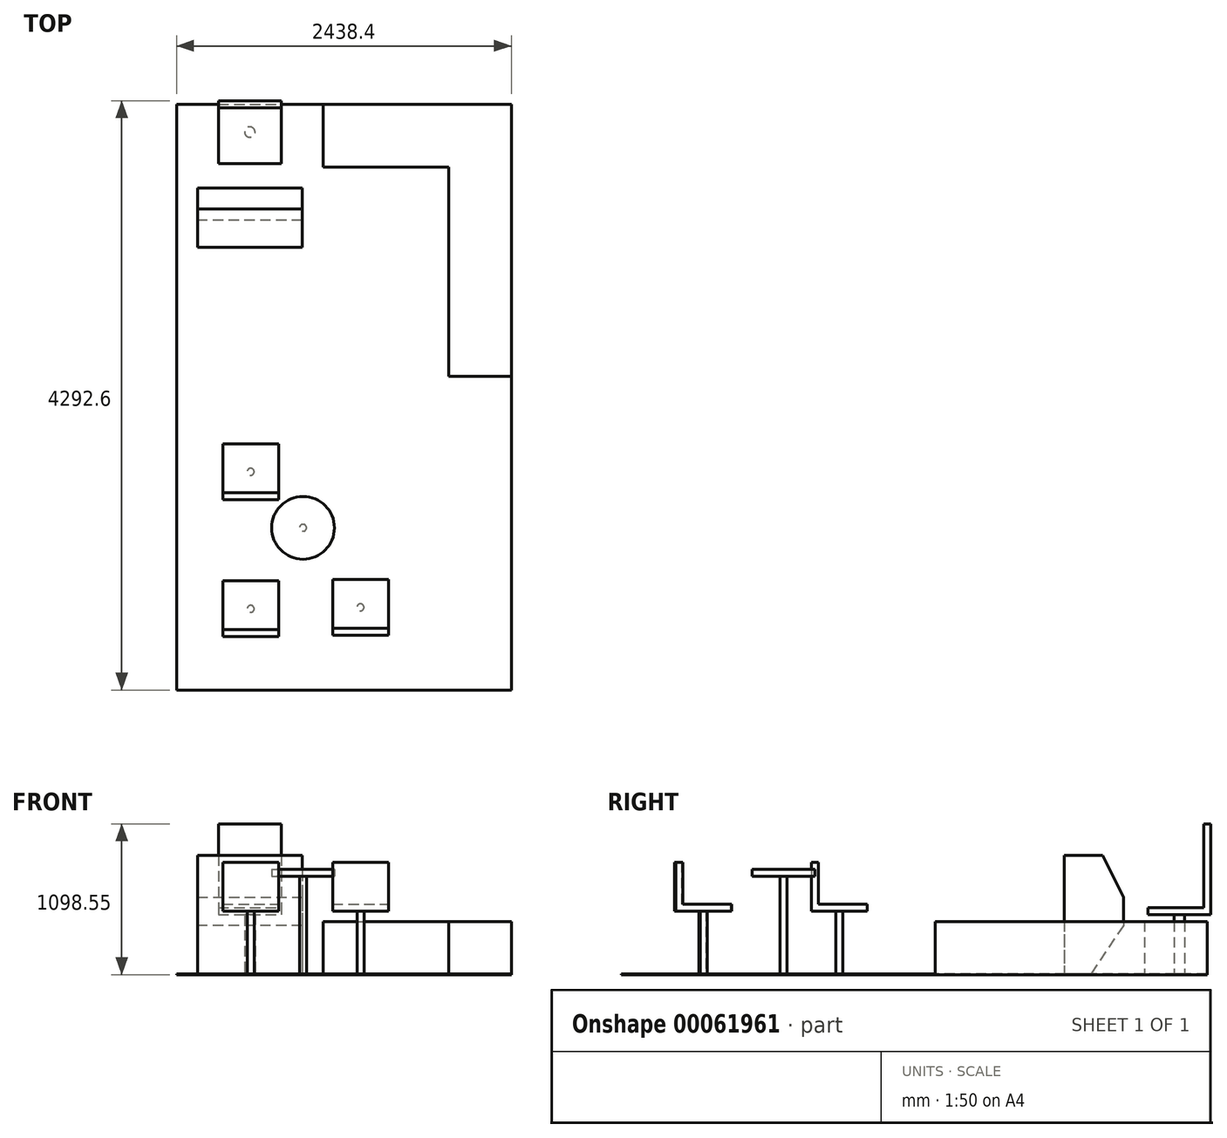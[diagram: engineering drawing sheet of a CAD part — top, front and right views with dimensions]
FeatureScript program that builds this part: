
annotation { "Feature Type Name" : "Feature", "Feature Type Description" : "" }
export const myFeature = defineFeature(function(context is Context, id is Id, definition is map)
    precondition{}
    {
        {
            var Q0;
            Q0=qCreatedBy(makeId("Top.planeOp"),FACE);
            var sketch = newSketch(context, id + "F0", { "sketchPlane" : qUnion([Q0])});
            skLineSegment(sketch, "E0.bottom", {"start": v(-2438.4, 4267.2) * mm, "end": v(0, 4267.2) * mm});
            skLineSegment(sketch, "E0.top", {"start": v(-2438.4, 0) * mm, "end": v(0, 0) * mm});
            skLineSegment(sketch, "E0.left", {"start": v(-2438.4, 4267.2) * mm, "end": v(-2438.4, 0) * mm});
            skLineSegment(sketch, "E0.right", {"start": v(0, 4267.2) * mm, "end": v(0, 0) * mm});
            skSolve(sketch);
        }
        {
            var Q0;
            Q0 = qSketchRegion(id + "F0", true);
            var Q1;
            Q1=makeQuery(id+"F0.imprint","IMPRINT",FACE,{"disambiguationData":[TD([[makeQuery(id+"F0.imprint","IMPRINT",EDGE,{"derivedFrom":sQuery(id+"F0.wireOp",EDGE,"E0.bottom")}),-1.0]])]});
            extrude(context, id + "F1", {"entities" : qUnion([Q0, Q1]), "depth" : 6.35 * mm});
        }
        {
            var Q0;
            Q0=makeQuery(id+"F1.opExtrude","CAP_FACE",FACE,{"disambiguationData":[OSD([sQuery(id+"F0.wireOp",EDGE,"E0.bottom"),sQuery(id+"F0.wireOp",EDGE,"E0.top"),sQuery(id+"F0.wireOp",EDGE,"E0.left"),sQuery(id+"F0.wireOp",EDGE,"E0.right")])],"isStart":false});
            var sketch = newSketch(context, id + "F2", { "sketchPlane" : qUnion([Q0])});
            skLineSegment(sketch, "E1.bottom", {"start": v(0, 4267.2) * mm, "end": v(-457.2, 4267.2) * mm});
            skLineSegment(sketch, "E1.top", {"start": v(0, 2286) * mm, "end": v(-457.2, 2286) * mm});
            skLineSegment(sketch, "E1.left", {"start": v(0, 4267.2) * mm, "end": v(0, 2286) * mm});
            skLineSegment(sketch, "E1.right", {"start": v(-457.2, 4267.2) * mm, "end": v(-457.2, 2286) * mm});
            skLineSegment(sketch, "E2.bottom", {"start": v(-1371.6, 4267.2) * mm, "end": v(-457.2, 4267.2) * mm});
            skLineSegment(sketch, "E2.top", {"start": v(-1371.6, 3810) * mm, "end": v(-457.2, 3810) * mm});
            skLineSegment(sketch, "E2.left", {"start": v(-1371.6, 4267.2) * mm, "end": v(-1371.6, 3810) * mm});
            skLineSegment(sketch, "E2.right", {"start": v(-457.2, 4267.2) * mm, "end": v(-457.2, 3810) * mm});
            skSolve(sketch);
        }
        {
            var Q0;
            Q0 = qSketchRegion(id + "F2", true);
            extrude(context, id + "F3", {"entities" : qUnion([Q0]), "operationType" : NewBodyOperationType.ADD, "depth" : 381 * mm});
        }
        {
            var Q0;
            Q0=makeQuery(id+"F1.opExtrude","CAP_FACE",FACE,{"disambiguationData":[OSD([sQuery(id+"F0.wireOp",EDGE,"E0.bottom"),sQuery(id+"F0.wireOp",EDGE,"E0.top"),sQuery(id+"F0.wireOp",EDGE,"E0.left"),sQuery(id+"F0.wireOp",EDGE,"E0.right")])],"isStart":false});
            var sketch = newSketch(context, id + "F4", { "sketchPlane" : qUnion([Q0])});
            skLineSegment(sketch, "E3.bottom", {"start": v(-2286, 3657.6) * mm, "end": v(-1524, 3657.6) * mm});
            skLineSegment(sketch, "E3.top", {"start": v(-2286, 3225.8) * mm, "end": v(-1524, 3225.8) * mm});
            skLineSegment(sketch, "E3.left", {"start": v(-2286, 3657.6) * mm, "end": v(-2286, 3225.8) * mm});
            skLineSegment(sketch, "E3.right", {"start": v(-1524, 3657.6) * mm, "end": v(-1524, 3225.8) * mm});
            skSolve(sketch);
        }
        {
            var Q0;
            Q0 = qSketchRegion(id + "F4", true);
            extrude(context, id + "F5", {"entities" : qUnion([Q0]), "operationType" : NewBodyOperationType.ADD, "depth" : 863.6 * mm});
        }
        {
            var Q0;
            Q0=makeQuery(id+"F5.opExtrude","CAP_EDGE",EDGE,{"disambiguationData":[OSD([sQuery(id+"F4.wireOp",EDGE,"E3.bottom")])],"isStart":false});
            chamfer(context, id + "F6", {"entities" : qUnion([Q0]), "chamferType" : ChamferType.TWO_OFFSETS, "width1" : 304.8 * mm, "oppositeDirection" : false, "width2" : 152.4 * mm, "tangentPropagation" : true});
        }
        {
            var Q0;
            Q0=makeQuery(id+"F5.opExtrude","SWEPT_FACE",FACE,{"disambiguationData":[OSD([sQuery(id+"F4.wireOp",EDGE,"E3.left")])]});
            var sketch = newSketch(context, id + "F7", { "sketchPlane" : qUnion([Q0])});
            skLineSegment(sketch, "E4.0", {"start": v(-3657.6, 565.15) * mm, "end": v(-3657.6, 6.35) * mm});
            skLineSegment(sketch, "E5.0", {"start": v(-3225.8, 869.95) * mm, "end": v(-3225.8, 6.35) * mm});
            skLineSegment(sketch, "E6.0", {"start": v(-3657.6, 6.35) * mm, "end": v(-3225.8, 6.35) * mm});
            skLineSegment(sketch, "E7", {"start": v(-3657.6, 356.85) * mm, "end": v(-3421.3, 6.35) * mm});
            skSolve(sketch);
        }
        {
            var Q0;
            {var subQ3=sQuery(id+"F7.wireOp",EDGE,"E7");Q0=makeQuery(id+"F7.imprint","IMPRINT",FACE,{"disambiguationData":[TD([[makeQuery(id+"F7.imprint","IMPRINT",EDGE,{"derivedFrom":subQ3}),-1.0]])]});}
            extrude(context, id + "F8", {"entities" : qUnion([Q0]), "operationType" : NewBodyOperationType.REMOVE, "oppositeDirection" : true, "depth" : 762 * mm});
        }
        {
            var Q0;
            Q0=makeQuery(id+"F8.boolean.opBoolean","MERGE",FACE,{"derivedFrom":[makeQuery(id+"F1.opExtrude","CAP_FACE",FACE,{"disambiguationData":[OSD([sQuery(id+"F0.wireOp",EDGE,"E0.bottom"),sQuery(id+"F0.wireOp",EDGE,"E0.top"),sQuery(id+"F0.wireOp",EDGE,"E0.left"),sQuery(id+"F0.wireOp",EDGE,"E0.right")])],"isStart":false}),makeQuery(id+"F8.opExtrude","SWEPT_FACE",FACE,{"disambiguationData":[OSD([sQuery(id+"F7.wireOp",EDGE,"E6.0")])]})]});
            var sketch = newSketch(context, id + "F9", { "sketchPlane" : qUnion([Q0])});
            skCircle(sketch, "E8", {"center": v(-1905, 4064) * mm, "radius": 38.1 * mm});
            skLineSegment(sketch, "E9", {"start": v(-1905, 3225.8) * mm, "end": v(-1905, 4064) * mm});
            skLineSegment(sketch, "E10.0", {"start": v(-1524, 3657.6) * mm, "end": v(-2286, 3657.6) * mm});
            skSolve(sketch);
        }
        {
            var Q0;
            Q0 = qSketchRegion(id + "F9", true);
            extrude(context, id + "F10", {"entities" : qUnion([Q0]), "operationType" : NewBodyOperationType.ADD, "depth" : 431.8 * mm});
        }
        {
            var Q0;
            Q0=makeQuery(id+"F10.opExtrude","CAP_FACE",FACE,{"disambiguationData":[OSD([sQuery(id+"F9.wireOp",EDGE,"E8")])],"isStart":false});
            var sketch = newSketch(context, id + "F11", { "sketchPlane" : qUnion([Q0])});
            skLineSegment(sketch, "E11.rect.bottom", {"start": v(-2133.6, 4292.6) * mm, "end": v(-1676.4, 4292.6) * mm});
            skLineSegment(sketch, "E11.rect.top", {"start": v(-2133.6, 3835.4) * mm, "end": v(-1676.4, 3835.4) * mm});
            skLineSegment(sketch, "E11.rect.left", {"start": v(-2133.6, 4292.6) * mm, "end": v(-2133.6, 3835.4) * mm});
            skLineSegment(sketch, "E11.rect.right", {"start": v(-1676.4, 4292.6) * mm, "end": v(-1676.4, 3835.4) * mm});
            skPoint(sketch, "E11.rect.middle", {"position": v(-1905, 4064) * mm});
            skSolve(sketch);
        }
        {
            var Q0;
            Q0 = qSketchRegion(id + "F11", true);
            extrude(context, id + "F12", {"entities" : qUnion([Q0]), "operationType" : NewBodyOperationType.ADD, "depth" : 50.8 * mm});
        }
        {
            var Q0;
            Q0=makeQuery(id+"F12.opExtrude","CAP_FACE",FACE,{"disambiguationData":[OSD([sQuery(id+"F11.wireOp",EDGE,"E11.rect.bottom"),sQuery(id+"F11.wireOp",EDGE,"E11.rect.top"),sQuery(id+"F11.wireOp",EDGE,"E11.rect.left"),sQuery(id+"F11.wireOp",EDGE,"E11.rect.right")])],"isStart":false});
            var sketch = newSketch(context, id + "F13", { "sketchPlane" : qUnion([Q0])});
            skLineSegment(sketch, "E12.bottom", {"start": v(-2133.6, 4292.6) * mm, "end": v(-1676.4, 4292.6) * mm});
            skLineSegment(sketch, "E12.top", {"start": v(-2133.6, 4241.8) * mm, "end": v(-1676.4, 4241.8) * mm});
            skLineSegment(sketch, "E12.left", {"start": v(-2133.6, 4292.6) * mm, "end": v(-2133.6, 4241.8) * mm});
            skLineSegment(sketch, "E12.right", {"start": v(-1676.4, 4292.6) * mm, "end": v(-1676.4, 4241.8) * mm});
            skSolve(sketch);
        }
        {
            var Q0;
            Q0 = qSketchRegion(id + "F13", true);
            extrude(context, id + "F14", {"entities" : qUnion([Q0]), "operationType" : NewBodyOperationType.ADD, "depth" : 609.6 * mm});
        }
        {
            var Q0;
            Q0=makeQuery(id+"F8.boolean.opBoolean","MERGE",FACE,{"derivedFrom":[makeQuery(id+"F1.opExtrude","CAP_FACE",FACE,{"disambiguationData":[OSD([sQuery(id+"F0.wireOp",EDGE,"E0.bottom"),sQuery(id+"F0.wireOp",EDGE,"E0.top"),sQuery(id+"F0.wireOp",EDGE,"E0.left"),sQuery(id+"F0.wireOp",EDGE,"E0.right")])],"isStart":false}),makeQuery(id+"F8.opExtrude","SWEPT_FACE",FACE,{"disambiguationData":[OSD([sQuery(id+"F7.wireOp",EDGE,"E6.0")])]})]});
            var sketch = newSketch(context, id + "F15", { "sketchPlane" : qUnion([Q0])});
            skCircle(sketch, "E13", {"center": v(-1898.37, 1589.52) * mm, "radius": 25.4 * mm});
            skCircle(sketch, "E14", {"center": v(-1098.7, 601.73) * mm, "radius": 25.4 * mm});
            skCircle(sketch, "E15", {"center": v(-1898.37, 590.79) * mm, "radius": 25.4 * mm});
            skLineSegment(sketch, "E16", {"start": v(-1898.37, 1589.52) * mm, "end": v(-1898.37, 590.79) * mm});
            skSolve(sketch);
        }
        {
            var Q0;
            Q0 = qSketchRegion(id + "F15", true);
            extrude(context, id + "F16", {"entities" : qUnion([Q0]), "operationType" : NewBodyOperationType.ADD, "depth" : 457.2 * mm});
        }
        {
            var Q0;
            Q0=makeQuery(id+"F16.opExtrude","CAP_FACE",FACE,{"disambiguationData":[OSD([sQuery(id+"F15.wireOp",EDGE,"E13")])],"isStart":false});
            var sketch = newSketch(context, id + "F17", { "sketchPlane" : qUnion([Q0])});
            skLineSegment(sketch, "E17.rect.bottom", {"start": v(-2101.57, 1792.72) * mm, "end": v(-1695.17, 1792.72) * mm});
            skLineSegment(sketch, "E17.rect.top", {"start": v(-2101.57, 1386.32) * mm, "end": v(-1695.17, 1386.32) * mm});
            skLineSegment(sketch, "E17.rect.left", {"start": v(-2101.57, 1792.72) * mm, "end": v(-2101.57, 1386.32) * mm});
            skLineSegment(sketch, "E17.rect.right", {"start": v(-1695.17, 1792.72) * mm, "end": v(-1695.17, 1386.32) * mm});
            skPoint(sketch, "E17.rect.middle", {"position": v(-1898.37, 1589.52) * mm});
            skCircle(sketch, "E18.0", {"center": v(-1098.7, 601.73) * mm, "radius": 25.4 * mm, "construction": true});
            skCircle(sketch, "E19.0", {"center": v(-1898.37, 590.79) * mm, "radius": 25.4 * mm, "construction": true});
            skLineSegment(sketch, "E20.rect.bottom", {"start": v(-2101.57, 793.99) * mm, "end": v(-1695.17, 793.99) * mm});
            skLineSegment(sketch, "E20.rect.top", {"start": v(-2101.57, 387.59) * mm, "end": v(-1695.17, 387.59) * mm});
            skLineSegment(sketch, "E20.rect.left", {"start": v(-2101.57, 793.99) * mm, "end": v(-2101.57, 387.59) * mm});
            skLineSegment(sketch, "E20.rect.right", {"start": v(-1695.17, 793.99) * mm, "end": v(-1695.17, 387.59) * mm});
            skLineSegment(sketch, "E21.rect.bottom", {"start": v(-1301.9, 804.93) * mm, "end": v(-895.5, 804.93) * mm});
            skLineSegment(sketch, "E21.rect.top", {"start": v(-1301.9, 398.53) * mm, "end": v(-895.5, 398.53) * mm});
            skLineSegment(sketch, "E21.rect.left", {"start": v(-1301.9, 804.93) * mm, "end": v(-1301.9, 398.53) * mm});
            skLineSegment(sketch, "E21.rect.right", {"start": v(-895.5, 804.93) * mm, "end": v(-895.5, 398.53) * mm});
            skSolve(sketch);
        }
        {
            var Q0;
            Q0 = qSketchRegion(id + "F17", true);
            extrude(context, id + "F18", {"entities" : qUnion([Q0]), "operationType" : NewBodyOperationType.ADD, "depth" : 50.8 * mm});
        }
        {
            var Q0;
            Q0=makeQuery(id+"F18.opExtrude","CAP_FACE",FACE,{"disambiguationData":[OSD([sQuery(id+"F17.wireOp",EDGE,"E20.rect.bottom"),sQuery(id+"F17.wireOp",EDGE,"E20.rect.top"),sQuery(id+"F17.wireOp",EDGE,"E20.rect.left"),sQuery(id+"F17.wireOp",EDGE,"E20.rect.right")])],"isStart":false});
            var sketch = newSketch(context, id + "F19", { "sketchPlane" : qUnion([Q0])});
            skLineSegment(sketch, "E22.bottom", {"start": v(-2101.57, 387.59) * mm, "end": v(-1695.17, 387.59) * mm});
            skLineSegment(sketch, "E22.top", {"start": v(-2101.57, 438.39) * mm, "end": v(-1695.17, 438.39) * mm});
            skLineSegment(sketch, "E22.left", {"start": v(-2101.57, 387.59) * mm, "end": v(-2101.57, 438.39) * mm});
            skLineSegment(sketch, "E22.right", {"start": v(-1695.17, 387.59) * mm, "end": v(-1695.17, 438.39) * mm});
            skLineSegment(sketch, "E23.0", {"start": v(-895.5, 804.93) * mm, "end": v(-895.5, 398.53) * mm});
            skLineSegment(sketch, "E23.1", {"start": v(-1301.9, 804.93) * mm, "end": v(-1301.9, 398.53) * mm});
            skLineSegment(sketch, "E23.2", {"start": v(-1301.9, 398.53) * mm, "end": v(-895.5, 398.53) * mm});
            skLineSegment(sketch, "E23.3", {"start": v(-2101.57, 1792.72) * mm, "end": v(-1695.17, 1792.72) * mm});
            skLineSegment(sketch, "E23.5", {"start": v(-1695.17, 1792.72) * mm, "end": v(-1695.17, 1386.32) * mm});
            skLineSegment(sketch, "E24.top", {"start": v(-1301.9, 449.33) * mm, "end": v(-895.5, 449.33) * mm});
            skLineSegment(sketch, "E24.left", {"start": v(-1301.9, 398.53) * mm, "end": v(-1301.9, 449.33) * mm});
            skLineSegment(sketch, "E24.right", {"start": v(-895.5, 398.53) * mm, "end": v(-895.5, 449.33) * mm});
            skLineSegment(sketch, "E25.bottom", {"start": v(-2101.57, 1386.32) * mm, "end": v(-1695.17, 1386.32) * mm});
            skLineSegment(sketch, "E25.top", {"start": v(-2101.57, 1437.12) * mm, "end": v(-1695.17, 1437.12) * mm});
            skLineSegment(sketch, "E25.left", {"start": v(-2101.57, 1386.32) * mm, "end": v(-2101.57, 1437.12) * mm});
            skLineSegment(sketch, "E25.right", {"start": v(-1695.17, 1386.32) * mm, "end": v(-1695.17, 1437.12) * mm});
            skSolve(sketch);
        }
        {
            var Q0;
            Q0 = qSketchRegion(id + "F19", true);
            extrude(context, id + "F20", {"entities" : qUnion([Q0]), "operationType" : NewBodyOperationType.ADD, "depth" : 304.8 * mm});
        }
        {
            var Q0;
            Q0=makeQuery(id+"F8.boolean.opBoolean","MERGE",FACE,{"derivedFrom":[makeQuery(id+"F1.opExtrude","CAP_FACE",FACE,{"disambiguationData":[OSD([sQuery(id+"F0.wireOp",EDGE,"E0.bottom"),sQuery(id+"F0.wireOp",EDGE,"E0.top"),sQuery(id+"F0.wireOp",EDGE,"E0.left"),sQuery(id+"F0.wireOp",EDGE,"E0.right")])],"isStart":false}),makeQuery(id+"F8.opExtrude","SWEPT_FACE",FACE,{"disambiguationData":[OSD([sQuery(id+"F7.wireOp",EDGE,"E6.0")])]})]});
            var sketch = newSketch(context, id + "F21", { "sketchPlane" : qUnion([Q0])});
            skCircle(sketch, "E26", {"center": v(-1517.15, 1181.14) * mm, "radius": 25.4 * mm});
            skSolve(sketch);
        }
        {
            var Q0;
            Q0 = qSketchRegion(id + "F21", true);
            extrude(context, id + "F22", {"entities" : qUnion([Q0]), "operationType" : NewBodyOperationType.ADD, "depth" : 711.2 * mm});
        }
        {
            var Q0;
            Q0=makeQuery(id+"F22.opExtrude","CAP_FACE",FACE,{"disambiguationData":[OSD([sQuery(id+"F21.wireOp",EDGE,"E26")])],"isStart":false});
            var sketch = newSketch(context, id + "F23", { "sketchPlane" : qUnion([Q0])});
            skCircle(sketch, "E27", {"center": v(-1517.15, 1181.14) * mm, "radius": 228.6 * mm});
            skSolve(sketch);
        }
        {
            var Q0;
            Q0 = qSketchRegion(id + "F23", true);
            extrude(context, id + "F24", {"entities" : qUnion([Q0]), "operationType" : NewBodyOperationType.ADD, "depth" : 50.8 * mm});
        }
    });
